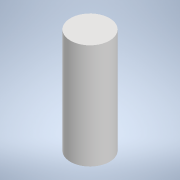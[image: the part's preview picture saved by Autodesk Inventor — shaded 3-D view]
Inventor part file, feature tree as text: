
AUTODESK INVENTOR PART (.ipt)
format: ipt  version: 2022 (Build 260153070, 153G)  size: 96,768 bytes
history: native  units: mm
features: extrude x1, shell x1, sketch x1
ambient origin geometry x8: Origin, YZ Plane, XZ Plane, XY Plane, X Axis, Y Axis, Z Axis, Center Point
bodies: Solid1 (feature_tree)
feature tree (3):
  extrude  "Extrusion1"  Depth=300.0mm TaperAngle=0.0deg
  shell  "Shell1"  Thickness=1.0mm
  sketch  "Sketch1"  dims[d0=110.0mm d1=300.0mm d2=0.0mm d3=1.0mm]
